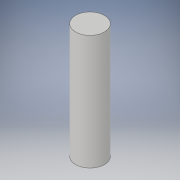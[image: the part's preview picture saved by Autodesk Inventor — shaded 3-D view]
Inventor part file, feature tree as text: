
AUTODESK INVENTOR PART (.ipt)
format: ipt  version: 2017.1 (Build 211199000, 199)  size: 88,576 bytes
history: native  units: in
note: dims shown in document units (in); Inventor stores cm internally (conversion verified against a paired STEP export)
features: extrude x1, sketch x1
ambient origin geometry x8: Origin, YZ Plane, XZ Plane, XY Plane, X Axis, Y Axis, Z Axis, Center Point
bodies: Solid1 (feature_tree)
feature tree (2):
  extrude  "Extrusion1"  Depth=2.0in TaperAngle=0.0deg
  sketch  "Sketch1"  dims[d0=0.502in d1=2.0in d2=0.0in]
